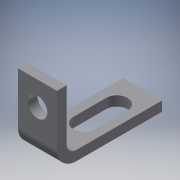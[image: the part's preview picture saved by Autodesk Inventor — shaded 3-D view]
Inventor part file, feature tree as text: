
AUTODESK INVENTOR PART (.ipt)
format: ipt  version: 2017 (Build 210142000, 142)  size: 141,824 bytes
history: native  units: in
note: dims shown in document units (in); Inventor stores cm internally (conversion verified against a paired STEP export)
features: sheet_metal_op x4, sketch x3, other x2, extrude x1
ambient origin geometry x8: Origin, YZ Plane, XZ Plane, XY Plane, X Axis, Y Axis, Z Axis, Center Point
bodies: Body1 (feature_tree)
feature tree (10):
  sheet_metal_op  "Face1"
  sheet_metal_op  "Flange1"
  extrude  "Extrusion3"  Depth=0.238in
  sketch  "Sketch1"  dims[d0=0.64in d1=0.238in]
  other  "Plate1"
  sketch  "Sketch2"  dims[d10=0.059in]
  other  "Plate2"
  sheet_metal_op  "Bend1"
  sheet_metal_op  "Corner1"
  sketch  "Sketch4"  dims[d11=0.059in d12=0.0295in d13=0.118in d14=0.059in d15=0.43in d16=90.0deg d17=0.059in d18=0.236in d19=0.059in d20=0.059in d22=0.12in d23=0.059in d24=0.0in d25=0.285in d27=0.13in d28=0.0655in d29=0.119in d30=0.2in d21=1.0in]
